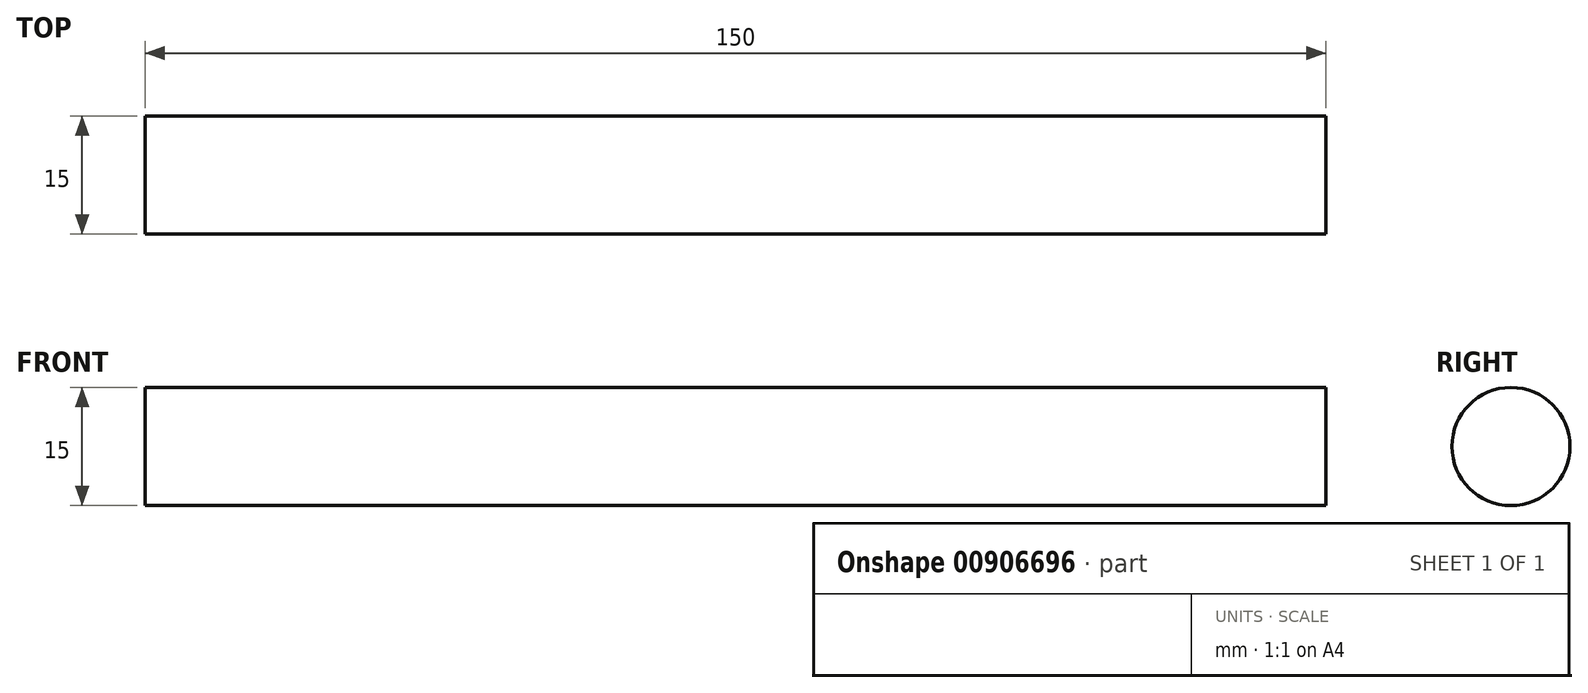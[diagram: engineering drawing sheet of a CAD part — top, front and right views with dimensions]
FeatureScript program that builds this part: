
annotation { "Feature Type Name" : "Feature", "Feature Type Description" : "" }
export const myFeature = defineFeature(function(context is Context, id is Id, definition is map)
    precondition{}
    {
        {
            var Q0;
            Q0=qCreatedBy(makeId("Front.planeOp"),FACE);
            var sketch = newSketch(context, id + "F0", { "sketchPlane" : qUnion([Q0])});
            skLineSegment(sketch, "E0", {"start": v(0, 0) * mm, "end": v(0, 7.5) * mm});
            skLineSegment(sketch, "E1", {"start": v(0, 7.5) * mm, "end": v(150, 7.5) * mm});
            skLineSegment(sketch, "E2", {"start": v(150, 7.5) * mm, "end": v(150, 0) * mm});
            skLineSegment(sketch, "E3", {"start": v(-29.83, 0) * mm, "end": v(169.8, 0) * mm, "construction": true});
            skLineSegment(sketch, "E4", {"start": v(0, 0) * mm, "end": v(150, 0) * mm});
            skSolve(sketch);
        }
        {
            var Q0;
            Q0=makeQuery(id+"F0.imprint","IMPRINT",FACE,{"disambiguationData":[TD([[makeQuery(id+"F0.imprint","IMPRINT",EDGE,{"derivedFrom":sQuery(id+"F0.wireOp",EDGE,"E0")}),-1.0]])]});
            var Q1;
            Q1=sQuery(id+"F0.wireOp",EDGE,"E3");
            revolve(context, id + "F1", {"surfaceOperationType" : NewSurfaceOperationType.NEW, "entities" : qUnion([Q0]), "axis" : qUnion([Q1]), "revolveType" : RevolveType.FULL});
        }
    });
